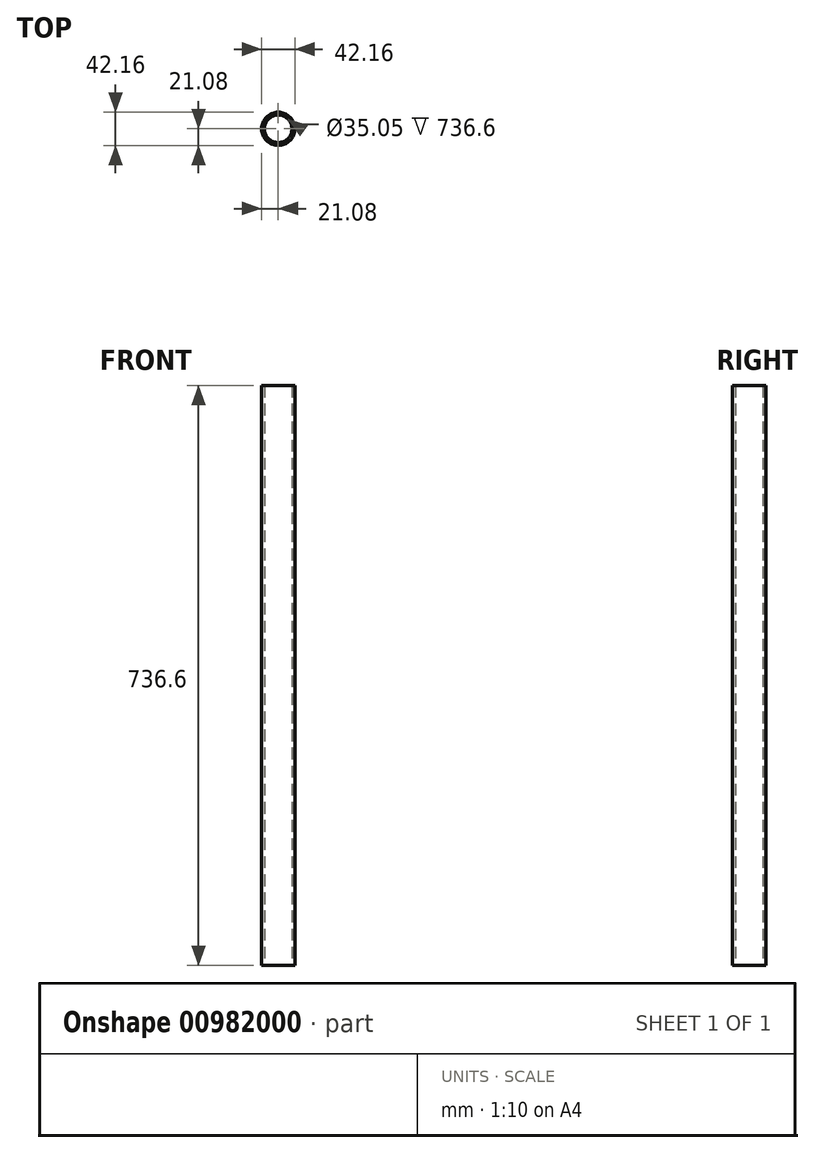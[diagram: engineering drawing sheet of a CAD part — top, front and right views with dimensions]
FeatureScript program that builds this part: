
annotation { "Feature Type Name" : "Feature", "Feature Type Description" : "" }
export const myFeature = defineFeature(function(context is Context, id is Id, definition is map)
    precondition{}
    {
        {
            var Q0;
            Q0=qCreatedBy(makeId("Top.planeOp"),FACE);
            var sketch = newSketch(context, id + "F0", { "sketchPlane" : qUnion([Q0])});
            skCircle(sketch, "E0", {"center": v(0, 0) * mm, "radius": 17.53 * mm});
            skCircle(sketch, "E1", {"center": v(0, 0) * mm, "radius": 21.08 * mm});
            skSolve(sketch);
        }
        {
            var Q0;
            Q0=qSketchRegion(id+"F0",true);
            extrude(context, id + "F1", {"entities" : qUnion([Q0]), "depth" : 736.6 * mm, "offsetDistance" : 25.4 * mm});
        }
    });
